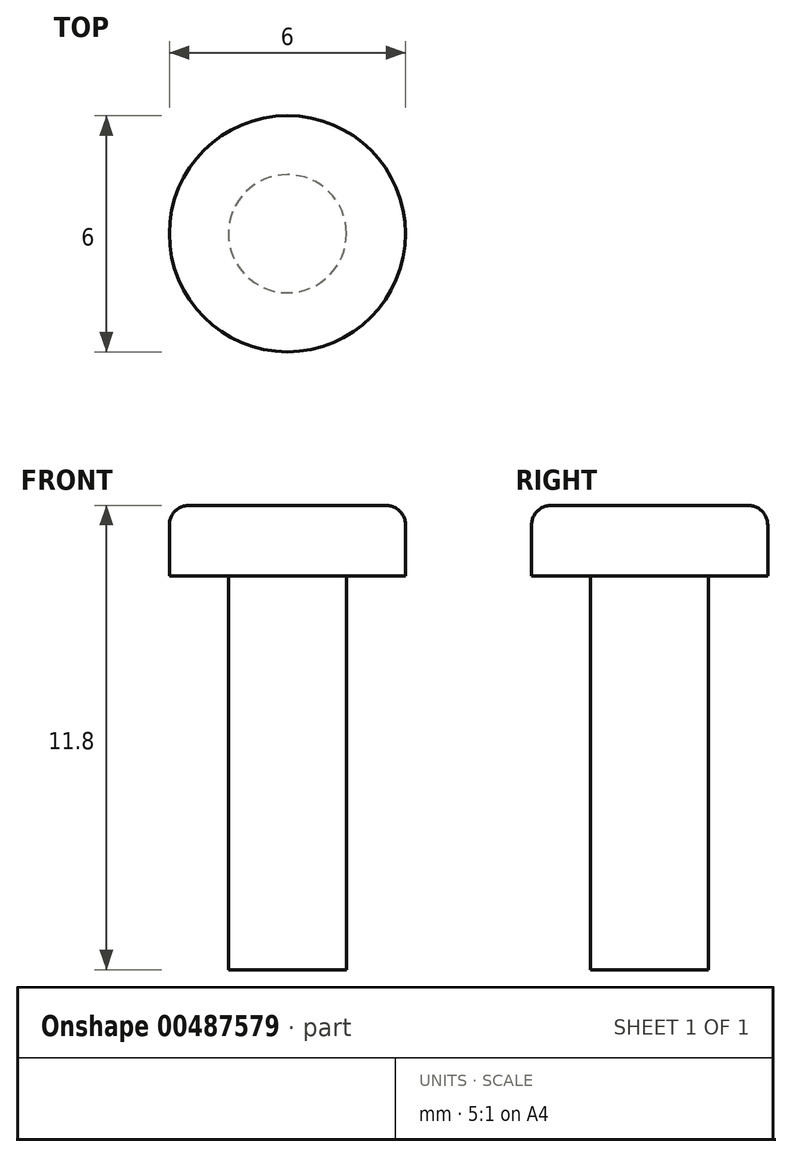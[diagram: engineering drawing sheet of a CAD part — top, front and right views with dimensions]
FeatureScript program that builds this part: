
annotation { "Feature Type Name" : "Feature", "Feature Type Description" : "" }
export const myFeature = defineFeature(function(context is Context, id is Id, definition is map)
    precondition{}
    {
        {
            var Q0;
            Q0=qCreatedBy(makeId("Top.planeOp"),FACE);
            var sketch = newSketch(context, id + "F0", { "sketchPlane" : qUnion([Q0])});
            skCircle(sketch, "E0", {"center": v(0, 0.55) * mm, "radius": 3 * mm});
            skSolve(sketch);
        }
        {
            var Q0;
            Q0 = qSketchRegion(id + "F0", true);
            extrude(context, id + "F1", {"entities" : qUnion([Q0]), "depth" : 1.8 * mm});
        }
        {
            var Q0;
            Q0=makeQuery(id+"F1.opExtrude","CAP_FACE",FACE,{"disambiguationData":[OSD([sQuery(id+"F0.wireOp",EDGE,"E0")])],"isStart":true});
            var sketch = newSketch(context, id + "F2", { "sketchPlane" : qUnion([Q0])});
            skCircle(sketch, "E1", {"center": v(0, -0.55) * mm, "radius": 1.5 * mm});
            skSolve(sketch);
        }
        {
            var Q0;
            Q0 = qSketchRegion(id + "F2", true);
            var Q1;
            Q1=makeQuery(id+"F2.imprint","IMPRINT",FACE,{"disambiguationData":[TD([[makeQuery(id+"F2.imprint","IMPRINT",EDGE,{"derivedFrom":sQuery(id+"F2.wireOp",EDGE,"E1")}),1.0]])]});
            extrude(context, id + "F3", {"entities" : qUnion([Q0, Q1]), "operationType" : NewBodyOperationType.ADD, "depth" : 10 * mm, "offsetDistance" : 25 * mm});
        }
        {
            var Q0;
            Q0=makeQuery(id+"F1.opExtrude","CAP_EDGE",EDGE,{"disambiguationData":[OSD([sQuery(id+"F0.wireOp",EDGE,"E0")])],"isStart":false});
            fillet(context, id + "F4", {"entities" : qUnion([Q0]), "radius" : 0.5 * mm, "tangentPropagation" : true, "allowEdgeOverflow" : false});
        }
    });
